# Revit family: IS_Connect_E7724_BIM_NL
name_source: partatom
category: Plumbing Fixtures
revit_build: Autodesk Revit MEP 2014 (Build: 20130308_1515(x64)
units: mm (PartAtom-declared; Revit-internal decimal feet)

## types (1)
- E772401 - CONNECT ZITING EN DEKSEL SC DUN
    Accessories = www.idealstandardnederland.nl
    AreaUnits = millimeters
    Assembly Code = C1030200
    AssetType = Vast
    BIMObjectName = ISI_IdealStandard_WcSeatsAndCovers_E772401
    BREEAMApproved = No
    BarCode = 5017830474807
    Brand = Ideal Standard
    CWFU = 0
    ConnectionType = Sanitair
    Cost = 0 $
    Default Elevation = 0 mm  [stored 0 ft]
    Description = Connect zitting en deksel dun softclosing.
    DurationUnit = jaar
    ECA = No
    ExpectedLife = 25
    Features = Zitting en deksel dun softclosing.
    Finish = Wit
    HWFU = 0
    IfcExportAs = IfcSanitaryTerminalType
    IfcExportType = TOILETPAN
    InstallationInstructions = http://www.idealstandardnederland.nl
    LinearUnits = millimeters
    ManufacturerURL = www.idealstandardnederland.nl
    Model = E772401
    ModelNumber = E772401
    ModelReference = Connect zitting en deksel dun softclosing.
    NBSDescription = WC seats and covers
    NBSReference = 45-35-70/391
    Name = WcSeatsAndCovers_E772401_IdealStandard
    NettWeight = 2.5 kg
    NominalDepth = 0 mm  [stored 0 ft]
    NominalHeight = 50 mm
    NominalLength = 430 mm
    NominalWidth = 365 mm
    PanColor = Wit
    PanMaterial = Duroplast
    ProductInformation = http://www.idealstandardnederland.nl
    Shape = Gesculptuurd
    Size = 365 x 430 x 50 mm
    Space = Internal
    SpilloverLevel = 0 mm  [stored 0 ft]
    ToiletPanType = WashDown
    ToiletType = Other
    URL = www.idealstandardnederland.nl
    Uniclass2015Code = Pr_40_20_93_95
    Uniclass2015Title = WC seats and covers
    Uniclass2015Version = Products v1.1
    Version = 1
    VolumeUnits = liter
    WFU = 0
    WRAS = No
    WarrantyDescription = Fabrieksgarantie
    WarrantyDurationParts = 5
    WarrantyDurationUnit = jaar
    WaterEfficientProduct = No

note: [stored X ft] marks values corroborated as IEEE doubles in the binary element streams (Revit-internal decimal feet)

## geometry (parser evidence)
native form markers: Sweep x2
no freeform markers — native parametric forms only
